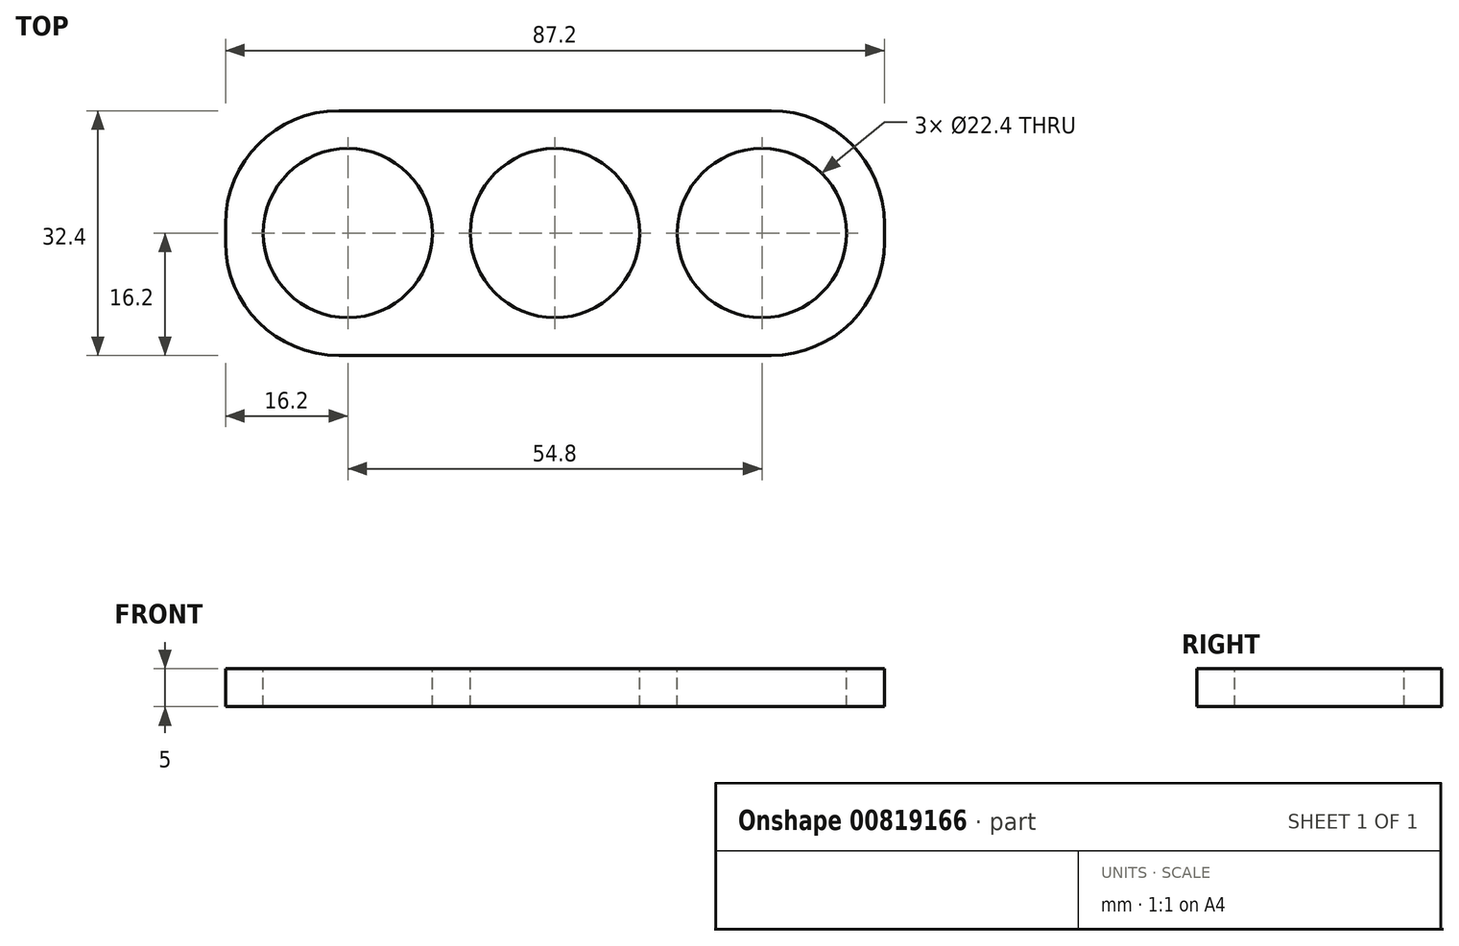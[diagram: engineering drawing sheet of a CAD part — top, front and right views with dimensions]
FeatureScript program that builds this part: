
annotation { "Feature Type Name" : "Feature", "Feature Type Description" : "" }
export const myFeature = defineFeature(function(context is Context, id is Id, definition is map)
    precondition{}
    {
        {
            var Q0;
            Q0=qCreatedBy(makeId("Top.planeOp"),FACE);
            var sketch = newSketch(context, id + "F0", { "sketchPlane" : qUnion([Q0])});
            skCircle(sketch, "E0", {"center": v(0, 0) * mm, "radius": 11.2 * mm});
            skCircle(sketch, "E1", {"center": v(27.4, 0) * mm, "radius": 11.2 * mm});
            skCircle(sketch, "E2", {"center": v(-27.4, 0) * mm, "radius": 11.2 * mm});
            skLineSegment(sketch, "E3.bottom", {"start": v(-28.6, 16.2) * mm, "end": v(28.6, 16.2) * mm});
            skLineSegment(sketch, "E3.top", {"start": v(-28.6, -16.2) * mm, "end": v(28.6, -16.2) * mm});
            skLineSegment(sketch, "E3.left", {"start": v(-43.6, 1.2) * mm, "end": v(-43.6, -1.2) * mm});
            skLineSegment(sketch, "E3.right", {"start": v(43.6, 1.2) * mm, "end": v(43.6, -1.2) * mm});
            skPoint(sketch, "E4.visualSharp", {"position": v(-43.6, 16.2) * mm});
            skArc(sketch, "E4.filletArc", {"start": v(-28.6, 16.2) * mm, "mid": v(-39.2, 11.8) * mm, "end": v(-43.6, 1.2) * mm});
            skPoint(sketch, "E5.visualSharp", {"position": v(-43.6, -16.2) * mm});
            skArc(sketch, "E5.filletArc", {"start": v(-43.6, -1.2) * mm, "mid": v(-39.2, -11.8) * mm, "end": v(-28.6, -16.2) * mm});
            skPoint(sketch, "E6.visualSharp", {"position": v(43.6, -16.2) * mm});
            skArc(sketch, "E6.filletArc", {"start": v(28.6, -16.2) * mm, "mid": v(39.2, -11.8) * mm, "end": v(43.6, -1.2) * mm});
            skPoint(sketch, "E7.visualSharp", {"position": v(43.6, 16.2) * mm});
            skArc(sketch, "E7.filletArc", {"start": v(43.6, 1.2) * mm, "mid": v(39.2, 11.8) * mm, "end": v(28.6, 16.2) * mm});
            skSolve(sketch);
        }
        {
            var Q0;
            Q0=makeQuery(id+"F0.imprint","IMPRINT",FACE,{"disambiguationData":[TD([[makeQuery(id+"F0.imprint","IMPRINT",EDGE,{"derivedFrom":sQuery(id+"F0.wireOp",EDGE,"E0")}),-1.0]])]});
            extrude(context, id + "F1", {"entities" : qUnion([Q0]), "oppositeDirection" : true, "depth" : 5 * mm, "offsetDistance" : 25 * mm});
        }
    });
